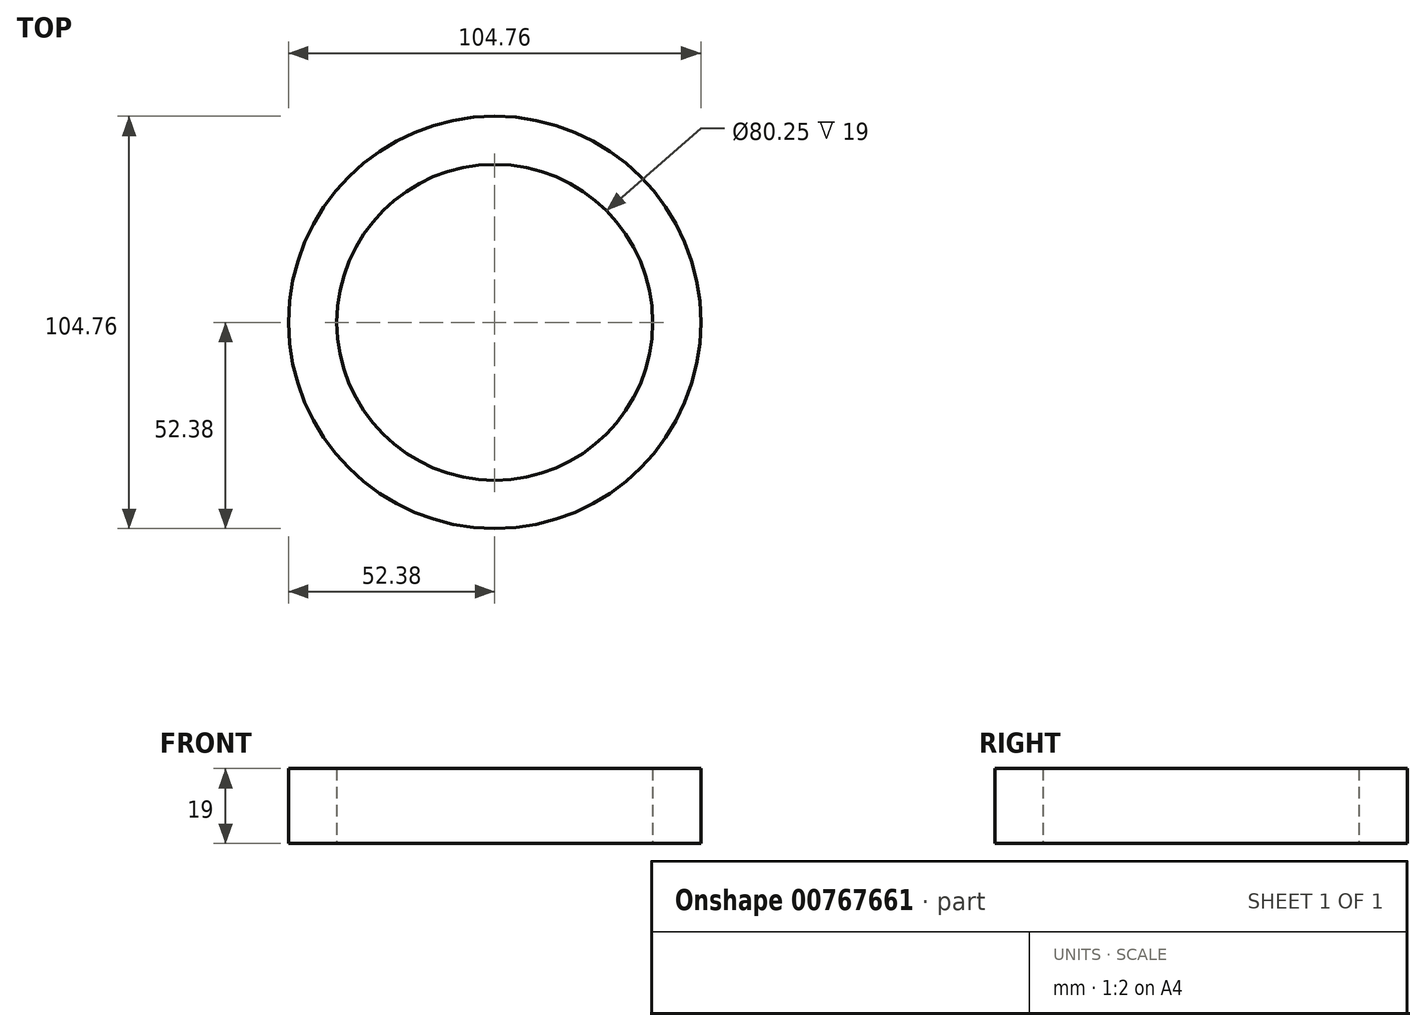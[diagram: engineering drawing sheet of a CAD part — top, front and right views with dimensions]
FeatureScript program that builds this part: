
annotation { "Feature Type Name" : "Feature", "Feature Type Description" : "" }
export const myFeature = defineFeature(function(context is Context, id is Id, definition is map)
    precondition{}
    {
        {
            var Q0;
            Q0=qCreatedBy(makeId("Top.planeOp"),FACE);
            var sketch = newSketch(context, id + "F0", { "sketchPlane" : qUnion([Q0])});
            skCircle(sketch, "E0", {"center": v(0, 0) * mm, "radius": 52.38 * mm});
            skCircle(sketch, "E1", {"center": v(0, 0) * mm, "radius": 40.12 * mm});
            skSolve(sketch);
        }
        {
            var Q0;
            Q0=makeQuery(id+"F0.imprint","IMPRINT",FACE,{"disambiguationData":[TD([[makeQuery(id+"F0.imprint","IMPRINT",EDGE,{"derivedFrom":sQuery(id+"F0.wireOp",EDGE,"E0")}),1.0]])]});
            extrude(context, id + "F1", {"entities" : qUnion([Q0]), "depth" : 19 * mm, "offsetDistance" : 25 * mm});
        }
    });
